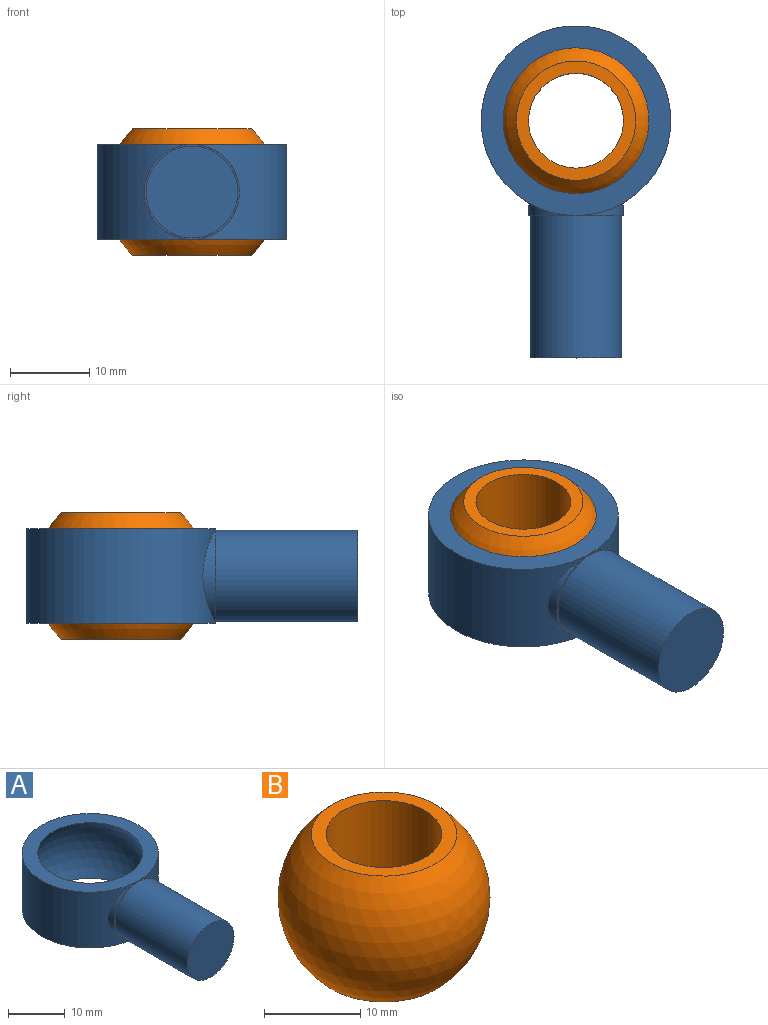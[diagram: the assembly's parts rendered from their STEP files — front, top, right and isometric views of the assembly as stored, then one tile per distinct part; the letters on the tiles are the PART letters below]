
ASSEMBLY  parts=2 mates=1
PART A: 9 faces, bbox 24x42x12 mm
  f0: cylinder r=6mm len=12mm, axis (0,1,0), area 14.9mm2, adj f1,f7
  f1: cylinder r=12mm len=24mm, axis (0,0,-1), area 787.8mm2, adj f0,f2,f3,f4
  f2: plane 24x24mm, normal (0,0,1), area 185.4mm2, adj f1,f5
  f3: plane 24x24mm, normal (0,0,-1), area 185.4mm2, adj f1,f5
  f4: cylinder r=6mm len=12mm, axis (0,1,0), area 14.9mm2, adj f1,f7
  f5: sphere r=11mm, area 829.4mm2, adj f2,f3
  f6: cylinder r=5.8mm len=18mm, axis (0,-1,0), area 656mm2, adj f7,f8
  f7: plane 12x12mm, normal (0,-1,0), area 7.4mm2, adj f0,f4,f6
  f8: plane 11.6x11.6mm, normal (0,-1,0), area 105.7mm2, adj f6
PART B: 4 faces, bbox 22x22x16 mm
  f0: cylinder r=6mm len=16mm, axis (0,0,1), area 603.2mm2, adj f1,f2
  f1: plane 15.1x15.1mm, normal (0,0,-1), area 66mm2, adj f0,f3
  f2: plane 15.1x15.1mm, normal (0,0,1), area 66mm2, adj f0,f3
  f3: sphere r=11mm, area 1105.8mm2, adj f1,f2
PLACE A t=(169.99,138.04,12.76)mm
PLACE B t=(169.99,196.57,12.76)mm
MATE ball A.f1 <-> B.f0  axis (0,0,1) through (-468.91,-241.68,18.76)mm
